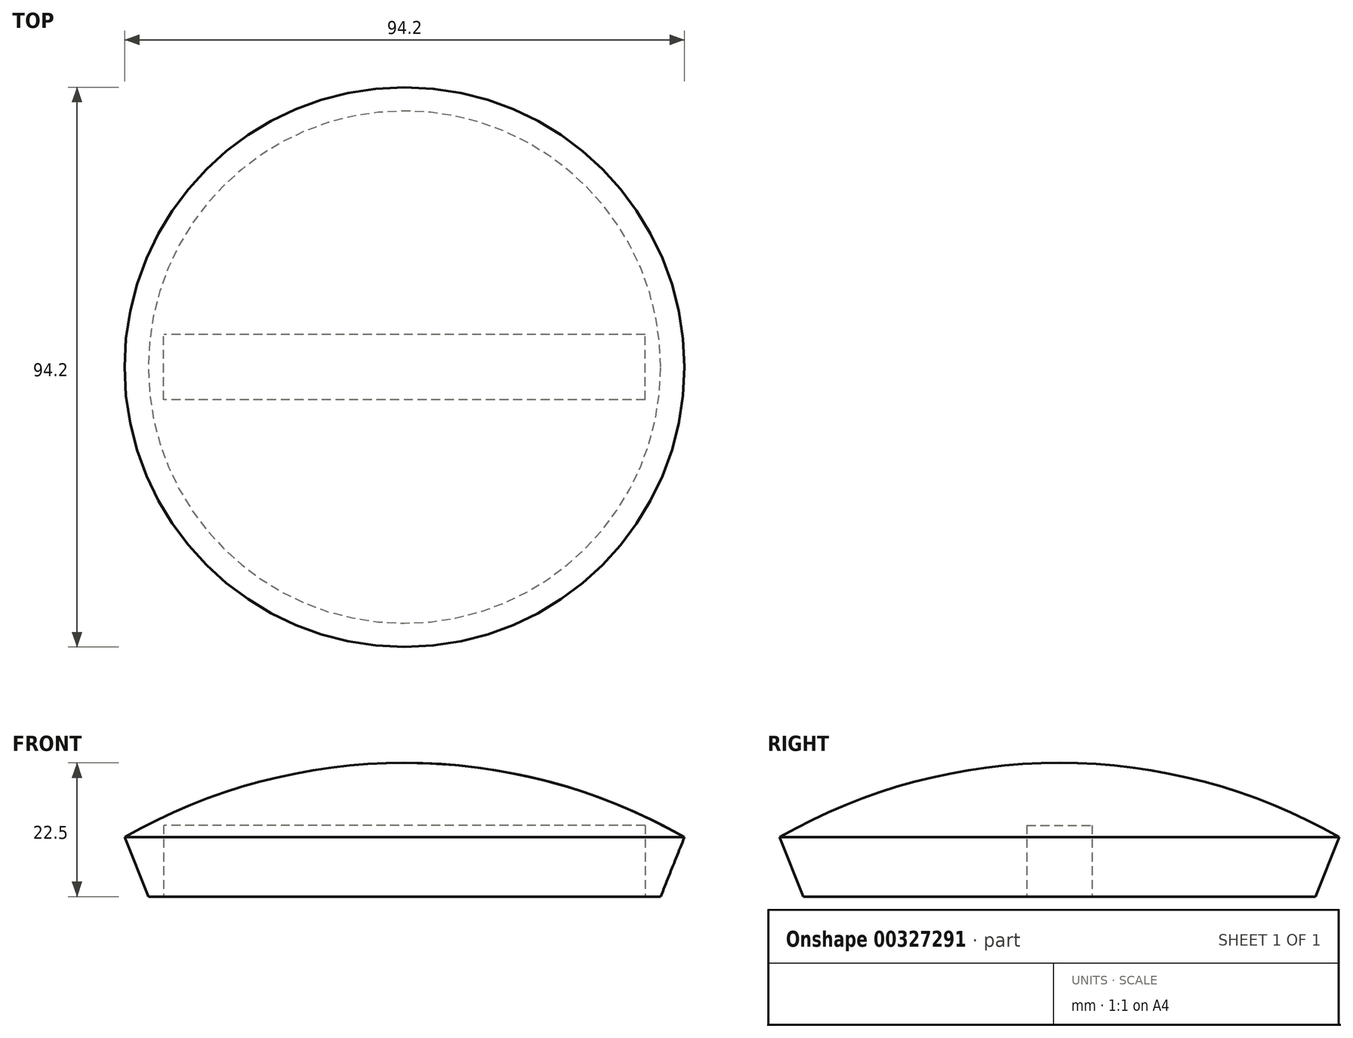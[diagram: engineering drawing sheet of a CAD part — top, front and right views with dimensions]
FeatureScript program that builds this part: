
annotation { "Feature Type Name" : "Feature", "Feature Type Description" : "" }
export const myFeature = defineFeature(function(context is Context, id is Id, definition is map)
    precondition{}
    {
        {
            var Q0;
            Q0=qCreatedBy(makeId("Top.planeOp"),FACE);
            var sketch = newSketch(context, id + "F0", { "sketchPlane" : qUnion([Q0])});
            skLineSegment(sketch, "E0.bottom", {"start": v(40.5, -5.5) * mm, "end": v(-40.5, -5.5) * mm});
            skLineSegment(sketch, "E0.top", {"start": v(40.5, 5.5) * mm, "end": v(-40.5, 5.5) * mm});
            skLineSegment(sketch, "E0.left", {"start": v(40.5, -5.5) * mm, "end": v(40.5, 5.5) * mm});
            skLineSegment(sketch, "E0.right", {"start": v(-40.5, -5.5) * mm, "end": v(-40.5, 5.5) * mm});
            skPoint(sketch, "E0.middle", {"position": v(0, 0) * mm});
            skLineSegment(sketch, "E1.bottom", {"start": v(42.1, 7.1) * mm, "end": v(-42.1, 7.1) * mm});
            skLineSegment(sketch, "E1.top", {"start": v(42.1, -7.1) * mm, "end": v(-42.1, -7.1) * mm});
            skLineSegment(sketch, "E1.left", {"start": v(42.1, 7.1) * mm, "end": v(42.1, -7.1) * mm});
            skLineSegment(sketch, "E1.right", {"start": v(-42.1, 7.1) * mm, "end": v(-42.1, -7.1) * mm});
            skSolve(sketch);
        }
        {
            var Q0;
            Q0=qCreatedBy(makeId("Front.planeOp"),FACE);
            var sketch = newSketch(context, id + "F1", { "sketchPlane" : qUnion([Q0])});
            skPoint(sketch, "E2.0", {"position": v(40.5, 0) * mm});
            skLineSegment(sketch, "E3", {"start": v(0, 0) * mm, "end": v(43.1, 0) * mm});
            skLineSegment(sketch, "E4", {"start": v(43.1, 0) * mm, "end": v(47.1, 10) * mm});
            skLineSegment(sketch, "E5", {"start": v(-16.64, 22.5) * mm, "end": v(17.99, 22.5) * mm, "construction": true});
            skArc(sketch, "E6", {"start": v(47.1, 10) * mm, "mid": v(24.37, 19.32) * mm, "end": v(0, 22.5) * mm});
            skLineSegment(sketch, "E7", {"start": v(0, 20.9) * mm, "end": v(0, 22.5) * mm});
            skLineSegment(sketch, "E8", {"start": v(0, 33.58) * mm, "end": v(0, -10.84) * mm, "construction": true});
            skLineSegment(sketch, "E9", {"start": v(41.5, 0) * mm, "end": v(45.2, 9.24) * mm});
            skArc(sketch, "E10", {"start": v(45.2, 9.24) * mm, "mid": v(23.34, 17.94) * mm, "end": v(0, 20.9) * mm});
            skLineSegment(sketch, "E11", {"start": v(0, 0) * mm, "end": v(0, 20.9) * mm});
            skSolve(sketch);
        }
        {
            var Q0;
            Q0 = qSketchRegion(id + "F1", true);
            var Q1;
            Q1=sQuery(id+"F1.wireOp",EDGE,"E8");
            revolve(context, id + "F2", {"entities" : qUnion([Q0]), "axis" : qUnion([Q1]), "revolveType" : RevolveType.FULL});
        }
        {
            var Q0;
            Q0=makeQuery(id+"F0.imprint","IMPRINT",FACE,{"disambiguationData":[TD([[makeQuery(id+"F0.imprint","IMPRINT",EDGE,{"derivedFrom":sQuery(id+"F0.wireOp",EDGE,"E0.bottom")}),-1.0]])]});
            extrude(context, id + "F3", {"entities" : qUnion([Q0]), "operationType" : NewBodyOperationType.REMOVE, "depth" : 12 * mm});
        }
    });
